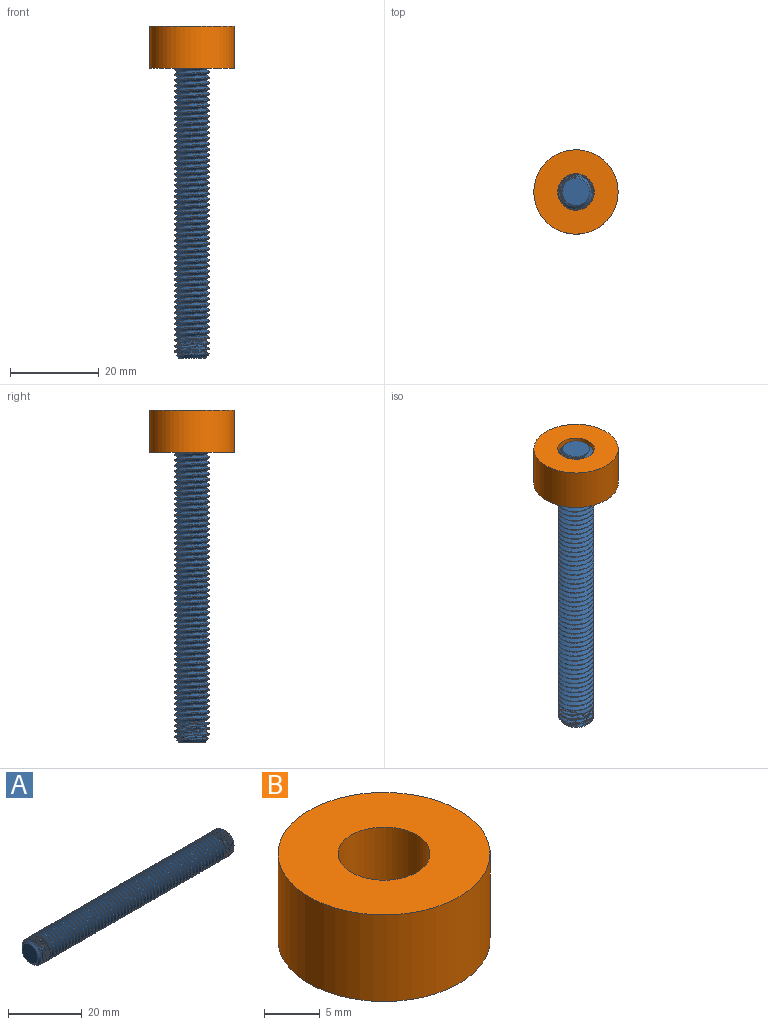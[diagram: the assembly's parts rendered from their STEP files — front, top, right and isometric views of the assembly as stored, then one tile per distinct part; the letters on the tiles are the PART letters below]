
ASSEMBLY  parts=2 mates=1
PART A: 9 faces, bbox 76x8.1x9.4 mm
  f0: cone r=4mm half-angle=45deg, axis (1,0,0), area 15.3mm2, adj f1,f4,f6,f7,f8
  f1: cone r=4mm half-angle=45deg, axis (1,0,0), area 0.8mm2, adj f0,f3,f6
  f2: cone r=3.06mm half-angle=45deg, axis (-1,0,0), area 16.1mm2, adj f3,f5,f6,f7,f8
  f3: cylinder r=4mm len=73.13mm, axis (1,0,0), area 1125.5mm2, adj f1,f2,f6,f8
  f4: plane 6.13x6.13mm, normal (-1,0,0), area 29.5mm2, adj f0
  f5: plane 6.13x6.13mm, normal (1,0,0), area 29.5mm2, adj f2
  f6: bspline ~75.51x9.39mm, area 1253.9mm2, adj f0,f1,f2,f3,f7
  f7: cylinder r=3.19mm len=74.75mm, axis (-1,0,0), area 1121.2mm2, adj f0,f2,f6,f8
  f8: bspline ~75.51x9.39mm, area 1253.1mm2, adj f0,f2,f3,f7
PART B: 4 faces, bbox 19.1x19.1x9.5 mm
  f0: plane 19.05x19.05mm, normal (0,0,1), area 231.5mm2, adj f2,f3
  f1: plane 19.05x19.05mm, normal (0,0,-1), area 231.5mm2, adj f2,f3
  f2: cylinder r=9.53mm len=19.05mm, axis (0,0,-1), area 570mm2, adj f0,f1
  f3: cylinder r=4.13mm len=9.53mm, axis (0,0,-1), area 247mm2, adj f0,f1
PLACE A rot(axis=(0,-1,0),90deg) t=(-10.56,-5.43,-31.73)mm
PLACE B t=(-10.56,-5.43,1.01)mm
MATE fastened A.f0 <-> B.f2  axis (0,0,1) through (-10.56,-5.43,5.77)mm
